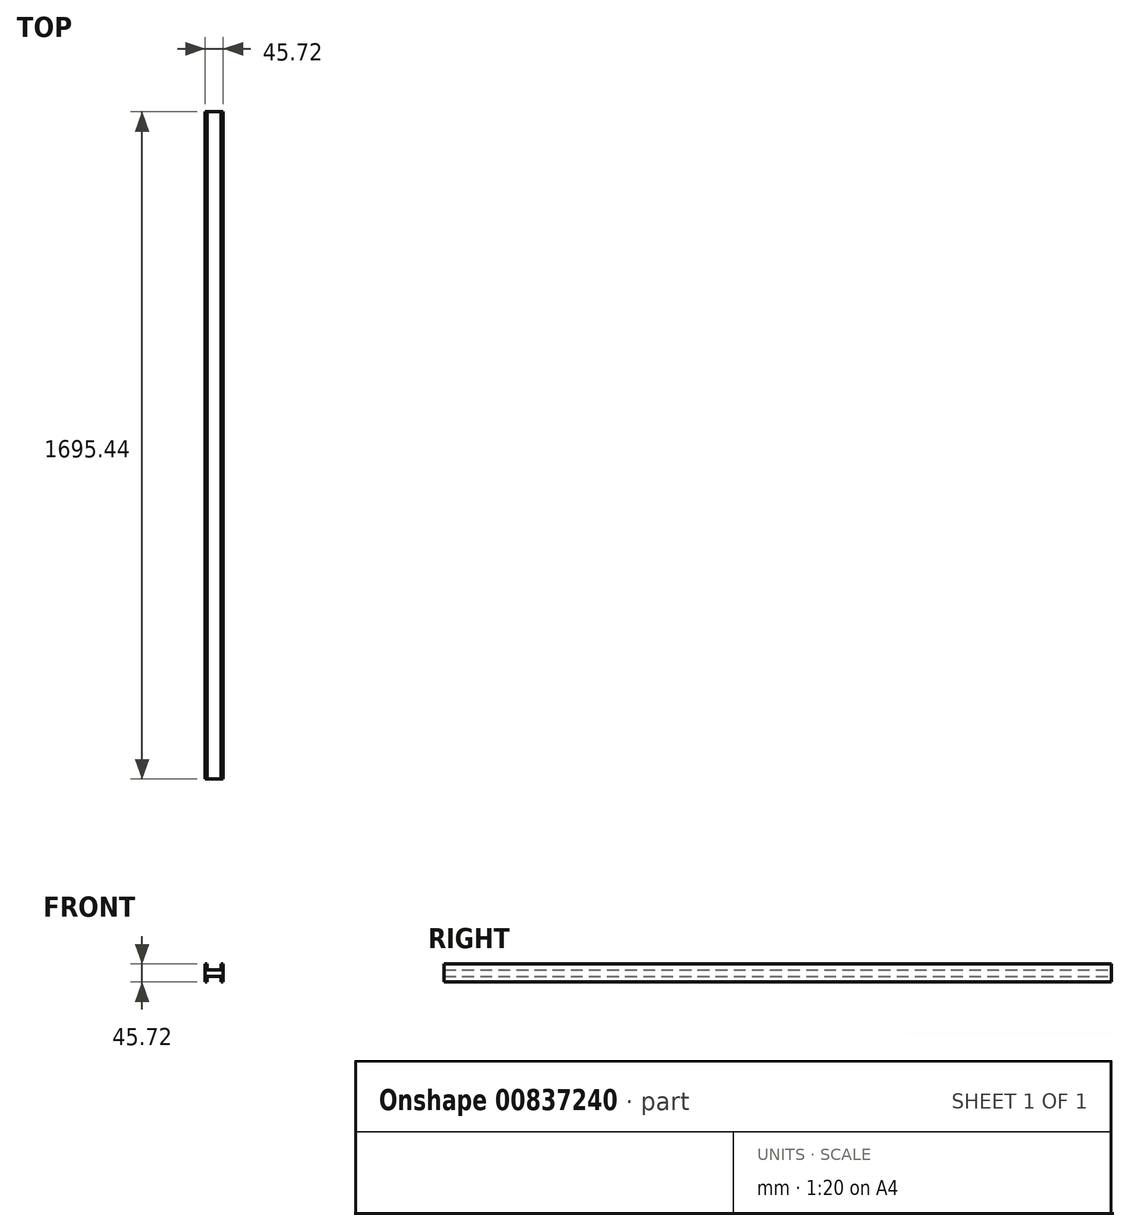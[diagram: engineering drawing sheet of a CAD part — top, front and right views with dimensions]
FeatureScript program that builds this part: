
annotation { "Feature Type Name" : "Feature", "Feature Type Description" : "" }
export const myFeature = defineFeature(function(context is Context, id is Id, definition is map)
    precondition{}
    {
        {
            var Q0;
            Q0=qCreatedBy(makeId("Front.planeOp"),FACE);
            var sketch = newSketch(context, id + "F0", { "sketchPlane" : qUnion([Q0])});
            skLineSegment(sketch, "E0.bottom", {"start": v(22.86, 22.86) * mm, "end": v(17.8, 22.86) * mm});
            skLineSegment(sketch, "E0.top", {"start": v(22.86, -22.86) * mm, "end": v(17.8, -22.86) * mm});
            skLineSegment(sketch, "E0.left", {"start": v(22.86, 22.86) * mm, "end": v(22.86, -22.86) * mm});
            skLineSegment(sketch, "E0.right", {"start": v(-22.86, 22.86) * mm, "end": v(-22.86, -22.86) * mm});
            skPoint(sketch, "E0.middle", {"position": v(0, 0) * mm});
            skLineSegment(sketch, "E1.top", {"start": v(-18.22, 8.64) * mm, "end": v(17.8, 8.64) * mm});
            skLineSegment(sketch, "E1.left", {"start": v(-18.22, 22.86) * mm, "end": v(-18.22, 8.64) * mm});
            skLineSegment(sketch, "E1.right", {"start": v(17.8, 22.86) * mm, "end": v(17.8, 8.64) * mm});
            skLineSegment(sketch, "E2", {"start": v(-65.42, 0) * mm, "end": v(65.2, 0) * mm, "construction": true});
            skLineSegment(sketch, "E3.MirrorCS", {"start": v(-18.22, -22.86) * mm, "end": v(-18.22, -8.64) * mm});
            skLineSegment(sketch, "E4.MirrorCS", {"start": v(-18.22, -8.64) * mm, "end": v(17.8, -8.64) * mm});
            skLineSegment(sketch, "E5.MirrorCS", {"start": v(17.8, -22.86) * mm, "end": v(17.8, -8.64) * mm});
            skLineSegment(sketch, "E6.trimOffspring", {"start": v(-18.22, 22.86) * mm, "end": v(-22.86, 22.86) * mm});
            skPoint(sketch, "E7.orphan", {"position": v(17.8, -31.29) * mm});
            skLineSegment(sketch, "E8.trimOffspring", {"start": v(-18.22, -22.86) * mm, "end": v(-22.86, -22.86) * mm});
            skPoint(sketch, "E9.orphan", {"position": v(-18.22, -31.29) * mm});
            skSolve(sketch);
        }
        {
            var Q0;
            Q0 = qSketchRegion(id + "F0", true);
            extrude(context, id + "F1", {"entities" : qUnion([Q0]), "endBound" : BoundingType.SYMMETRIC, "depth" : 1695.45 * mm, "offsetDistance" : 25.4 * mm});
        }
    });
